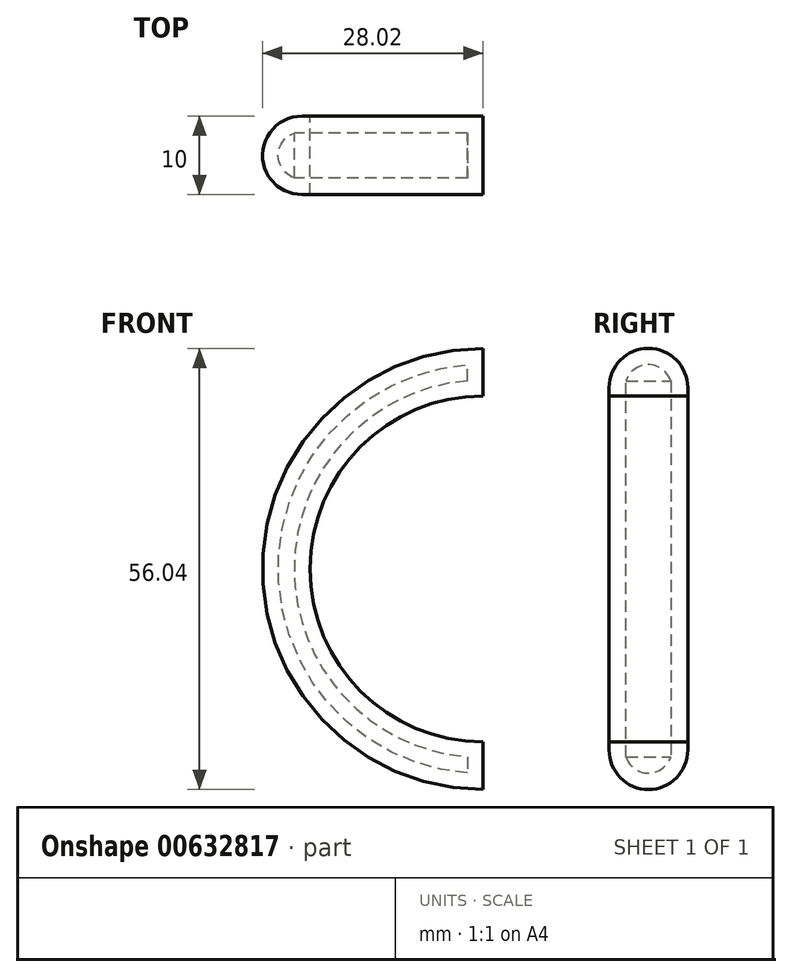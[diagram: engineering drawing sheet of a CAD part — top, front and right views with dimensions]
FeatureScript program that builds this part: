
annotation { "Feature Type Name" : "Feature", "Feature Type Description" : "" }
export const myFeature = defineFeature(function(context is Context, id is Id, definition is map)
    precondition{}
    {
        {
            var Q0;
            Q0=qCreatedBy(makeId("Front.planeOp"),FACE);
            var sketch = newSketch(context, id + "F0", { "sketchPlane" : qUnion([Q0])});
            skArc(sketch, "E0", {"start": v(0, 74.65) * mm, "mid": v(-28.02, 46.63) * mm, "end": v(0, 18.6) * mm});
            skArc(sketch, "E1", {"start": v(0, 68.6) * mm, "mid": v(-21.98, 46.63) * mm, "end": v(0, 24.65) * mm});
            skLineSegment(sketch, "E2", {"start": v(0, 74.65) * mm, "end": v(0, 18.6) * mm});
            skSolve(sketch);
        }
        {
            var Q0;
            {var subQ0=sQuery(id+"F0.wireOp",EDGE,"E0");Q0=makeQuery(id+"F0.imprint","IMPRINT",FACE,{"disambiguationData":[TD([[makeQuery(id+"F0.imprint","IMPRINT",EDGE,{"derivedFrom":subQ0}),1.0]])]});}
            extrude(context, id + "F1", {"entities" : qUnion([Q0]), "depth" : 10 * mm, "offsetDistance" : 25 * mm});
        }
        {
            var Q0;
            Q0=makeQuery(id+"F1.opExtrude","CAP_EDGE",EDGE,{"disambiguationData":[OSD([sQuery(id+"F0.wireOp",EDGE,"E0")])],"isStart":false});
            var Q1;
            Q1=makeQuery(id+"F1.opExtrude","CAP_EDGE",EDGE,{"disambiguationData":[OSD([sQuery(id+"F0.wireOp",EDGE,"E0")])],"isStart":true});
            fillet(context, id + "F2", {"entities" : qUnion([Q0, Q1]), "radius" : 5 * mm, "tangentPropagation" : true, "allowEdgeOverflow" : false});
        }
        {
            var Q0;
            Q0=makeQuery(id+"F2.opFillet","BLEND_FACE",FACE,{"disambiguationData":[OSD([sQuery(id+"F0.wireOp",EDGE,"E0")])]});
            var Q1;
            Q1=makeQuery(id+"F1.opExtrude","SWEPT_BODY",BODY,{"disambiguationData":[OSD([sQuery(id+"F0.wireOp",EDGE,"E0"),sQuery(id+"F0.wireOp",EDGE,"E1"),sQuery(id+"F0.wireOp",EDGE,"E2")])]});
            shell(context, id + "F3", {"isHollow" : true, "entities" : qUnion([Q0]), "parts" : qUnion([Q1]), "thickness" : 2 * mm});
        }
    });
